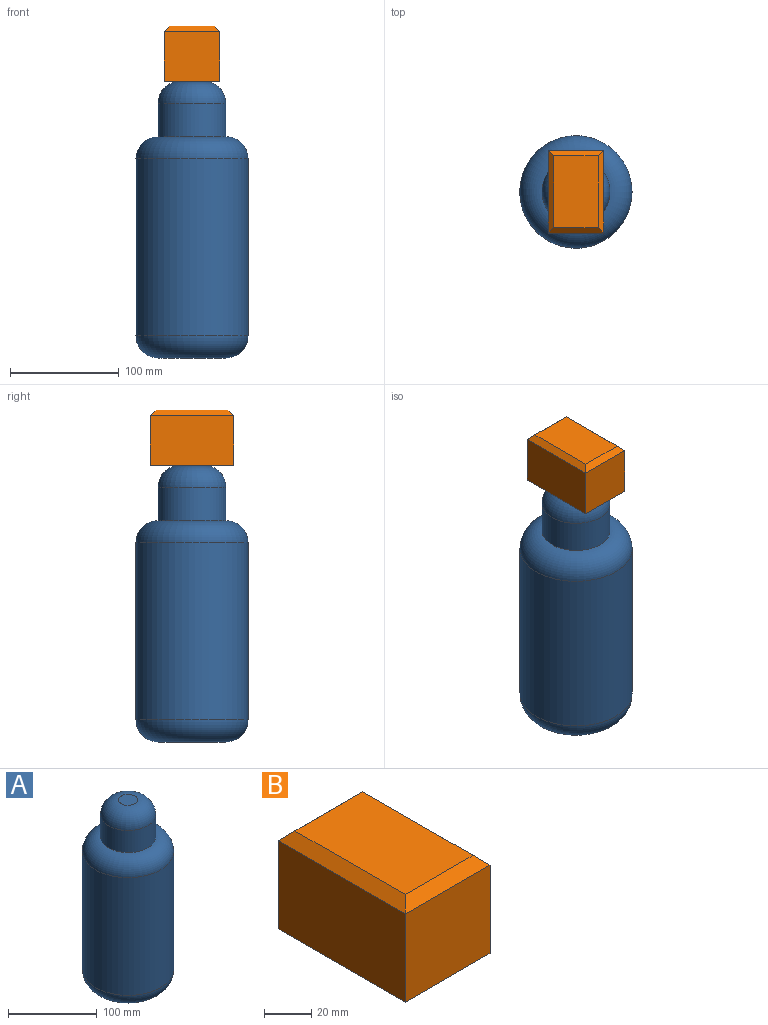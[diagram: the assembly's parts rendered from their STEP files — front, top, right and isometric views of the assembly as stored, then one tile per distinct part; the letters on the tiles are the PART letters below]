
ASSEMBLY  parts=2 mates=1
PART A: 7 faces, bbox 111.5x111.5x254 mm
  f0: cylinder r=51.5mm len=162.56mm, axis (0,0,-1), area 52597mm2, adj f2,f3
  f1: plane 62.35x62.35mm, normal (0,0,-1), area 3053.3mm2, adj f2
  f2: torus R=31.18mm, axis (0,0,1), area 8846.6mm2, adj f0,f1
  f3: torus R=31.18mm, axis (0,0,1), area 8846.6mm2, adj f0,f4
  f4: cylinder r=31.18mm len=62.35mm, axis (0,0,-1), area 5970.4mm2, adj f3,f6
  f5: plane 21.71x21.71mm, normal (0,0,1), area 370.2mm2, adj f6
  f6: torus R=10.86mm, axis (0,0,1), area 4771.4mm2, adj f4,f5
PART B: 10 faces, bbox 50.8x76.2x50.8 mm
  f0: plane 76.2x45.72mm, normal (1,0,0), area 3483.9mm2, adj f1,f3,f5,f7
  f1: plane 50.8x45.72mm, normal (0,1,0), area 2322.6mm2, adj f0,f2,f5,f9
  f2: plane 76.2x45.72mm, normal (-1,0,0), area 3483.9mm2, adj f1,f3,f5,f8
  f3: plane 50.8x45.72mm, normal (0,-1,0), area 2322.6mm2, adj f0,f2,f5,f6
  f4: plane 66.04x40.64mm, normal (0,0,1), area 2683.9mm2, adj f6,f7,f8,f9
  f5: plane 76.2x50.8mm, normal (0,0,-1), area 3871mm2, adj f0,f1,f2,f3
  f6: plane 50.8x5.08mm, normal (0,-0.71,0.71), area 328.5mm2, adj f3,f4,f7,f8
  f7: plane 76.2x5.08mm, normal (0.71,0,0.71), area 510.9mm2, adj f0,f4,f6,f9
  f8: plane 76.2x5.08mm, normal (-0.71,0,0.71), area 510.9mm2, adj f2,f4,f6,f9
  f9: plane 50.8x5.08mm, normal (0,0.71,0.71), area 328.5mm2, adj f1,f4,f7,f8
PLACE A t=(-120.8,-3.9,-28.22)mm fixed
PLACE B t=(-120.8,-3.9,225.78)mm
MATE fastened B.f5 <-> A.f0  axis (0,0,-1) through (-120.8,-3.9,225.78)mm
